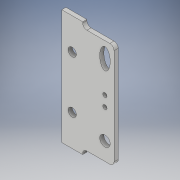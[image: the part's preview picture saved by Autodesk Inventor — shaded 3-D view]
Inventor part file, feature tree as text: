
AUTODESK INVENTOR PART (.ipt)
format: ipt  version: 2019 (Build 230136000, 136)  size: 138,752 bytes
history: native  units: mm
features: extrude x1, sketch x1
ambient origin geometry x8: Origin, YZ Plane, XZ Plane, XY Plane, X Axis, Y Axis, Z Axis, Center Point
bodies: Solid1 (feature_tree)
feature tree (2):
  extrude  "Extrusion1"  Depth=50.0mm
  sketch  "Sketch1"  dims[d1=55.0mm d3=50.0mm d6=2.0mm d7=2.0mm d8=2.0mm d9=4.0mm d10=5.0mm d11=5.0mm d12=2.0mm d13=2.0mm d21=2.0mm d22=0.0mm d23=4.0mm d24=25.0mm d26=12.5mm d27=5.0mm d28=5.0mm]
